# Revit family: Genie_Site_ArticulatingBoom_(S-45XC)a
name_source: partatom
category: Site
revit_build: Autodesk Revit 2018 (Build: 20190510_1515(x64)
units: mm (PartAtom-declared; Revit-internal decimal feet)

## family parameters
Always vertical = Yes
Cut with Voids When Loaded = No
OmniClass Number = 23.50.85.17
OmniClass Title = Telescoping Platforms
Part Type = Normal
Round Connector Dimension = Use Diameter
Shared = No
Work Plane-Based = No

## types (1)
- S-45 XC
    Assembly Code = E1030900
    AssetType = Moveable
    BIMObjectName = Genie_Site_ArticulatingBoom_(S-45XC)
    ClassificationName = Uniclass2015
    ClassificationValue = Pr_65_80_47_95
    Color = Grey & Blue
    Cost = 0 $
    Description = The Genie® S-40 XC™ and S-45 XC™ telescopic booms are engineered to work in more applications that require higher capacities. With industry-leading dual lift capacity — 660-lb (300 kg)/1,000-lb (454 kg) — a smooth operating envelope, this new XC boom lift is a perfect fit for your customers’ heavy lifting in construction, bridge inspections and maintenance, stadium and sports arena, gas and oil refineries, industrial, telecommunications and utility applications.
    DocumentationLiterature = https://www.genielift.com
    DocumentationTechnical = https://www.genielift.com
    DurationUnit = Years
    ExpectedLife = 0
    Features = The Genie® S-40 XC™ and S-45 XC™ telescopic booms are engineered to work in more applications that require higher capacities. With industry-leading dual lift capacity — 660-lb (300 kg)/1,000-lb (454 kg) — a smooth operating envelope, this new XC boom lift is a perfect fit for your customers’ heavy lifting in construction, bridge inspections and maintenance, stadium and sports arena, gas and oil refineries, industrial, telecommunications and utility applications.
    Finish = Painted Steel
    IfcExportAs = IfcTransportElement
    IfcExportType = IfcTransportElementType
    Keynote = X
    Manufacturer = Genie
    ManufacturerName = Genie
    Material = Painted Steel
    Model = Genie - Articulating Boom
    ModelNumber = S-45 XC
    ModelReference = Genie - Articulating Boom
    NBSDescription = Vertical lifting platforms
    NBSObjectName = Genie - Vertical lifting platforms
    NBSReference = 90-80-65/350
    NominalDepth = 2490 mm
    NominalHeight = 2510 mm  [stored 8.23491 ft]
    NominalLength = 8000 mm  [stored 26.2467 ft]
    ProductionYear = 2020
    Size = 8.0m x 2.51m x 2.49m
    Type Comments = S-45 XC
    TypeName = Genie - Articulating Boom
    URL = http://www.genielift.co.uk
    WarrantyDurationLabor = 0
    WarrantyDurationParts = 0
    WarrantyDurationUnit = Years
    WarrantyGuarantorLabor = http://www.genielift.co.uk
    WarrantyGuarantorParts = http://www.genielift.co.uk
    _BSBibleVersion = 16
    _BimSpecGuid = 0
    _CurrentRevision = 1
    _DistributedBy = www.bimstore.co

note: [stored X ft] marks values corroborated as IEEE doubles in the binary element streams (Revit-internal decimal feet)

## geometry (parser evidence)
native form markers: Sweep x20
no freeform markers — native parametric forms only
